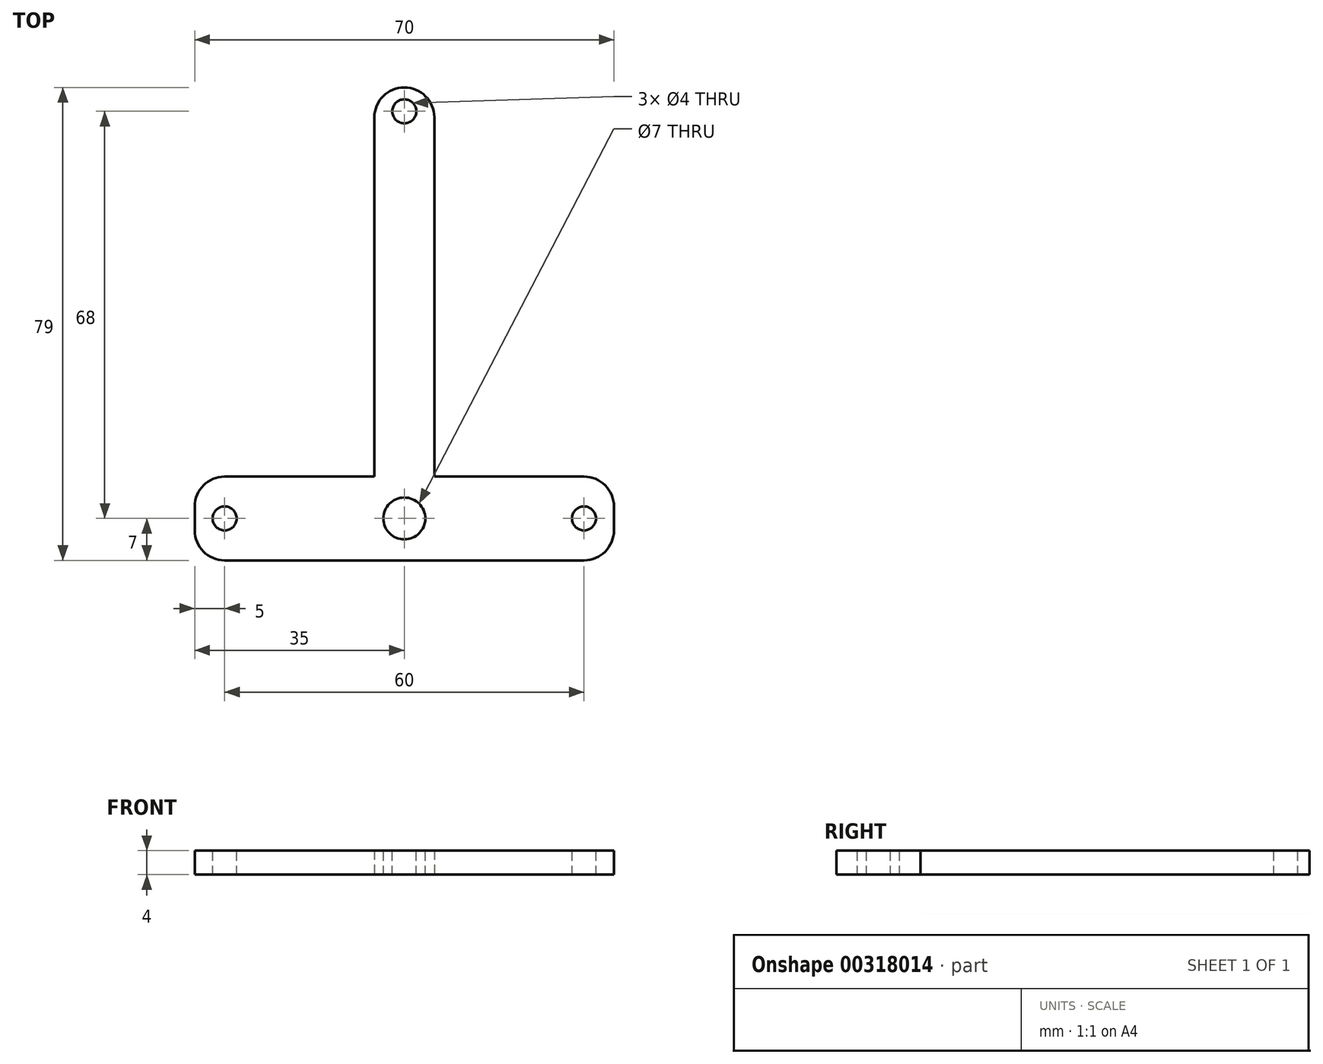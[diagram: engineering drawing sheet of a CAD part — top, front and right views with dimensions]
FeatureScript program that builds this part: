
annotation { "Feature Type Name" : "Feature", "Feature Type Description" : "" }
export const myFeature = defineFeature(function(context is Context, id is Id, definition is map)
    precondition{}
    {
        {
            var Q0;
            Q0=qCreatedBy(makeId("Top.planeOp"),FACE);
            var sketch = newSketch(context, id + "F0", { "sketchPlane" : qUnion([Q0])});
            skLineSegment(sketch, "E0", {"start": v(-5, 0) * mm, "end": v(-5, 65) * mm});
            skLineSegment(sketch, "E1", {"start": v(-5, 65) * mm, "end": v(5, 65) * mm});
            skLineSegment(sketch, "E2", {"start": v(5, 65) * mm, "end": v(5, 0) * mm});
            skLineSegment(sketch, "E3", {"start": v(5, 0) * mm, "end": v(35, 0) * mm});
            skLineSegment(sketch, "E4", {"start": v(35, 0) * mm, "end": v(35, -14) * mm});
            skLineSegment(sketch, "E5", {"start": v(35, -14) * mm, "end": v(-35, -14) * mm});
            skLineSegment(sketch, "E6", {"start": v(-35, -14) * mm, "end": v(-35, 0) * mm});
            skLineSegment(sketch, "E7", {"start": v(-35, 0) * mm, "end": v(-5, 0) * mm});
            skSolve(sketch);
        }
        {
            var Q0;
            Q0 = qSketchRegion(id + "F0", true);
            extrude(context, id + "F1", {"entities" : qUnion([Q0]), "depth" : 4 * mm});
        }
        {
            var Q0;
            Q0=makeQuery(id+"F1.opExtrude","CAP_FACE",FACE,{"disambiguationData":[OSD([sQuery(id+"F0.wireOp",EDGE,"E0"),sQuery(id+"F0.wireOp",EDGE,"E1"),sQuery(id+"F0.wireOp",EDGE,"E2"),sQuery(id+"F0.wireOp",EDGE,"E3"),sQuery(id+"F0.wireOp",EDGE,"E4"),sQuery(id+"F0.wireOp",EDGE,"E5"),sQuery(id+"F0.wireOp",EDGE,"E6"),sQuery(id+"F0.wireOp",EDGE,"E7")])],"isStart":false});
            var sketch = newSketch(context, id + "F2", { "sketchPlane" : qUnion([Q0])});
            skCircle(sketch, "E8", {"center": v(-30, -7) * mm, "radius": 2 * mm});
            skPoint(sketch, "E8.centerSnap0", {"position": v(-35, -7) * mm});
            skCircle(sketch, "E9", {"center": v(30, -7) * mm, "radius": 2 * mm});
            skPoint(sketch, "E9.centerSnap0", {"position": v(35, -7) * mm});
            skCircle(sketch, "E10", {"center": v(0, -7) * mm, "radius": 3.5 * mm});
            skCircle(sketch, "E11", {"center": v(0, 61) * mm, "radius": 2 * mm});
            skSolve(sketch);
        }
        {
            var Q0;
            Q0 = qSketchRegion(id + "F2", true);
            extrude(context, id + "F3", {"entities" : qUnion([Q0]), "operationType" : NewBodyOperationType.REMOVE, "oppositeDirection" : true, "depth" : 25 * mm});
        }
        {
            var Q0;
            Q0=makeQuery(id+"F1.opExtrude","SWEPT_EDGE",EDGE,{"disambiguationData":[OSD([sQuery(id+"F0.wireOp",EDGE,"E5"),sQuery(id+"F0.wireOp",EDGE,"E6")])]});
            var Q1;
            Q1=makeQuery(id+"F1.opExtrude","SWEPT_EDGE",EDGE,{"disambiguationData":[OSD([sQuery(id+"F0.wireOp",EDGE,"E6"),sQuery(id+"F0.wireOp",EDGE,"E7")])]});
            var Q2;
            Q2=makeQuery(id+"F1.opExtrude","SWEPT_EDGE",EDGE,{"disambiguationData":[OSD([sQuery(id+"F0.wireOp",EDGE,"E4"),sQuery(id+"F0.wireOp",EDGE,"E5")])]});
            var Q3;
            Q3=makeQuery(id+"F1.opExtrude","SWEPT_EDGE",EDGE,{"disambiguationData":[OSD([sQuery(id+"F0.wireOp",EDGE,"E3"),sQuery(id+"F0.wireOp",EDGE,"E4")])]});
            var Q4;
            Q4=makeQuery(id+"F1.opExtrude","SWEPT_EDGE",EDGE,{"disambiguationData":[OSD([sQuery(id+"F0.wireOp",EDGE,"E1"),sQuery(id+"F0.wireOp",EDGE,"E2")])]});
            var Q5;
            Q5=makeQuery(id+"F1.opExtrude","SWEPT_EDGE",EDGE,{"disambiguationData":[OSD([sQuery(id+"F0.wireOp",EDGE,"E0"),sQuery(id+"F0.wireOp",EDGE,"E1")])]});
            fillet(context, id + "F4", {"entities" : qUnion([Q0, Q1, Q2, Q3, Q4, Q5]), "radius" : 5 * mm, "tangentPropagation" : true, "allowEdgeOverflow" : false});
        }
    });
